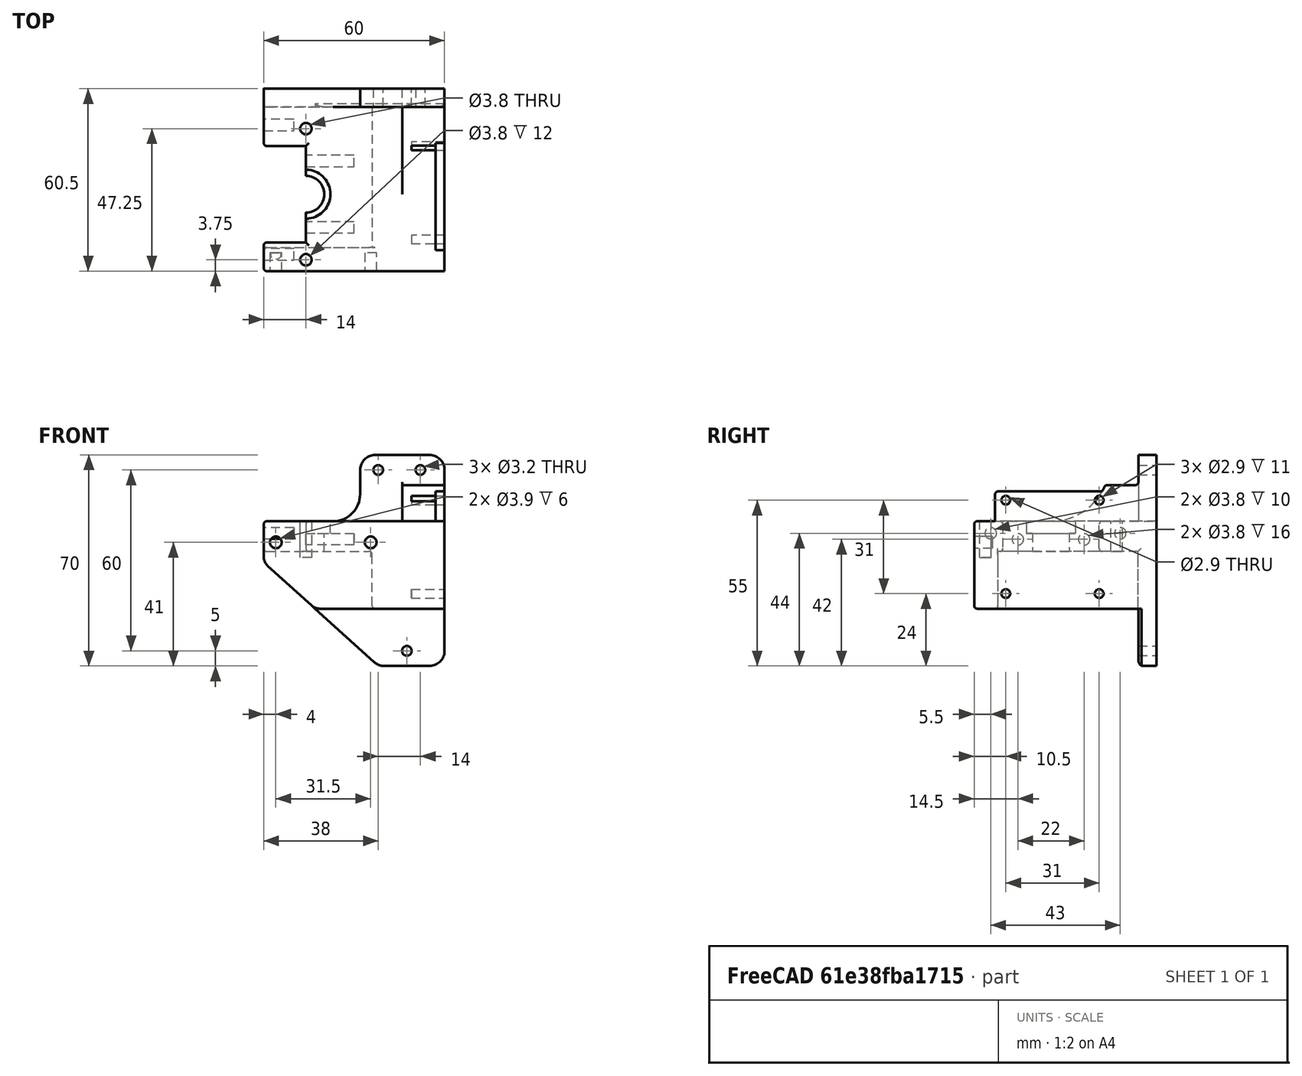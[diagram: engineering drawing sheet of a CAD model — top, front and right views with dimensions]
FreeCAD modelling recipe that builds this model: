
FCSTD DOCUMENT  (FreeCAD 0.19R)
Label: head9.3
License: All rights reserved
LicenseURL: http://en.wikipedia.org/wiki/All_rights_reserved
objects: PartDesign::Fillet×19, Sketcher::SketchObject×17, PartDesign::Pocket×15, PartDesign::Pad×2, PartDesign::Chamfer×1, PartDesign::Body×1, Mesh::Feature×1
note: 92 computed .brp shape members not serialized (recipe doc carries the construction recipe); baked Part::Feature solids carry a one-line shape summary decoded from their .brp

FEATURE [Sketcher::SketchObject] Sketch
  FullyConstrained = true
  MapMode = 5
  Support = -> [XY_Plane]
  sketch-geometry (5):
    g0: LineSegment StartX=0 StartY=0 StartZ=0 EndX=46 EndY=0 EndZ=0
    g1: LineSegment StartX=-14 StartY=0 StartZ=0 EndX=0 EndY=0 EndZ=0
    g2: LineSegment StartX=-14 StartY=0 StartZ=0 EndX=-14 EndY=-60.5 EndZ=0
    g3: LineSegment StartX=-14 StartY=-60.5 StartZ=0 EndX=46 EndY=-60.5 EndZ=0
    g4: LineSegment StartX=46 StartY=-60.5 StartZ=0 EndX=46 EndY=0 EndZ=0
  constraints (14):
    c: Coincident(g-1,g0)
    c: PointOnObject(g0,g-1)
    c: PointOnObject(g1,g-1)
    c: Coincident(g1,g0)
    c: Coincident(g1,g2)
    c: Vertical(g2)
    c: Coincident(g2,g3)
    c: Horizontal(g3)
    c: Coincident(g3,g4)
    c: Coincident(g4,g0)
    c: Vertical(g4)
    c: Distance(g4) = 60.5
    c: DistanceX(g0) = 46
    c: DistanceX(g1) = -14
FEATURE [PartDesign::Pad] Pad
  Direction = (1,1,1)
  Length = 70
  Length2 = 100
  Profile = -> Sketch
  Type = 0
FEATURE [Sketcher::SketchObject] Sketch002  label="platformnotch"
  FullyConstrained = false
  MapMode = 5
  Placement = pos=(0,0,70) rot=(0,0,1;0rad)
  Support = -> [Pad]
  sketch-geometry (6):
    g0: LineSegment StartX=32 StartY=-6 StartZ=0 EndX=32 EndY=-65.096 EndZ=0
    g1: LineSegment StartX=32 StartY=-65.096 StartZ=0 EndX=-40.7834 EndY=-65.096 EndZ=0
    g2: LineSegment StartX=-40.7834 StartY=-65.096 StartZ=0 EndX=-40.7834 EndY=12.9948 EndZ=0
    g3: LineSegment StartX=-40.7834 StartY=12.9948 StartZ=0 EndX=18 EndY=12.9948 EndZ=0
    g4: LineSegment StartX=18 StartY=12.9948 StartZ=0 EndX=18 EndY=-6 EndZ=0
    g5: LineSegment StartX=18 StartY=-6 StartZ=0 EndX=32 EndY=-6 EndZ=0
  constraints (15):
    c: Coincident(g0,g1)
    c: Coincident(g1,g2)
    c: Horizontal(g1)
    c: Vertical(g0)
    c: Vertical(g2)
    c: DistanceX(g0) = 32
    c: DistanceY(g0) = -6
    c: Coincident(g2,g3)
    c: Horizontal(g3)
    c: Coincident(g3,g4)
    c: Coincident(g4,g5)
    c: Coincident(g5,g0)
    c: Horizontal(g5)
    c: Vertical(g4)
    c: DistanceX(g3) = 18
FEATURE [PartDesign::Pocket] Pocket
  BaseFeature = -> Pad
  Length = 22
  Length2 = 100
  Profile = -> Sketch002
  Type = 0
FEATURE [Sketcher::SketchObject] Sketch008  label="pcbnotches"
  FullyConstrained = false
  MapMode = 5
  Placement = pos=(46,0,0) rot=(0.57735,0.57735,0.57735;2.0944rad)
  Support = -> [Pocket]
  sketch-geometry (8):
    g0: LineSegment StartX=-67.659 StartY=19 StartZ=0 EndX=-6 EndY=19 EndZ=0
    g1: LineSegment StartX=-6 StartY=19 StartZ=0 EndX=-6 EndY=-22.4626 EndZ=0
    g2: LineSegment StartX=-6 StartY=-22.4626 StartZ=0 EndX=-67.659 EndY=-22.4626 EndZ=0
    g3: LineSegment StartX=-67.659 StartY=-22.4626 StartZ=0 EndX=-67.659 EndY=19 EndZ=0
    g4: LineSegment StartX=-66.332 StartY=73.6841 StartZ=0 EndX=-6 EndY=73.6841 EndZ=0
    g5: LineSegment StartX=-6 StartY=73.6841 StartZ=0 EndX=-6 EndY=60 EndZ=0
    g6: LineSegment StartX=-6 StartY=60 StartZ=0 EndX=-66.332 EndY=60 EndZ=0
    g7: LineSegment StartX=-66.332 StartY=60 StartZ=0 EndX=-66.332 EndY=73.6841 EndZ=0
  constraints (20):
    c: Coincident(g0,g1)
    c: Coincident(g1,g2)
    c: Coincident(g2,g3)
    c: Coincident(g3,g0)
    c: Horizontal(g0)
    c: Horizontal(g2)
    c: Vertical(g1)
    c: Vertical(g3)
    c: DistanceY(g0) = 19
    c: Coincident(g4,g5)
    c: Coincident(g5,g6)
    c: Coincident(g6,g7)
    c: Coincident(g7,g4)
    c: Horizontal(g4)
    c: Horizontal(g6)
    c: Vertical(g5)
    c: Vertical(g7)
    c: DistanceX(g4) = -6
    c: DistanceY(g5) = 60
    c: DistanceX(g0) = -6
FEATURE [PartDesign::Pocket] Pocket001
  BaseFeature = -> Pocket
  Length = 76
  Length2 = 100
  Profile = -> Sketch008
  Type = 0
FEATURE [Sketcher::SketchObject] Sketch003  label="extredureholes"
  FullyConstrained = true
  MapMode = 5
  Placement = pos=(0,0,48) rot=(0,0,1;0rad)
  Support = -> [Pocket001]
  sketch-geometry (3):
    g0: Circle CenterX=0 CenterY=-13.25 CenterZ=0 NormalX=0 NormalY=0 NormalZ=1 AngleXU=0 Radius=1.9
    g1: Circle CenterX=0 CenterY=-56.75 CenterZ=0 NormalX=0 NormalY=0 NormalZ=1 AngleXU=0 Radius=1.9
    g2: LineSegment StartX=-14.87 StartY=-35 StartZ=0 EndX=14.87 EndY=-35 EndZ=0
  constraints (8):
    c: Distance(g1,g0) = 43.5
    c: Diameter(g1) = 3.8
    c: PointOnObject(g0,g-2)
    c: Symmetric(g2,g2,g-2)
    c: Distance(g2) = 29.74
    c: Symmetric(g1,g0,g2)
    c: DistanceY(g2) = -35
    c: Diameter(g0) = 3.8
FEATURE [PartDesign::Pocket] Pocket002
  BaseFeature = -> Pocket001
  Length = 12
  Length2 = 100
  Profile = -> Sketch003
  Type = 0
FEATURE [Sketcher::SketchObject] Sketch004  label="topNotch"
  FullyConstrained = true
  MapMode = 5
  Placement = pos=(0,0,48) rot=(0,0,1;0rad)
  Support = -> [Pocket002]
  sketch-geometry (4):
    g0: ArcOfCircle CenterX=0 CenterY=-35 CenterZ=0 NormalX=0 NormalY=0 NormalZ=1 AngleXU=0 Radius=8.125 StartAngle=4.71239 EndAngle=7.85398
    g1: LineSegment StartX=-1.5e-15 StartY=-43.125 StartZ=0 EndX=-25 EndY=-43.125 EndZ=0
    g2: LineSegment StartX=-25 StartY=-43.125 StartZ=0 EndX=-25 EndY=-26.875 EndZ=0
    g3: LineSegment StartX=-25 StartY=-26.875 StartZ=0 EndX=-2.629e-13 EndY=-26.875 EndZ=0
  constraints (11):
    c: PointOnObject(g0,g-2)
    c: Diameter(g0) = 16.25
    c: DistanceY(g0) = -35
    c: Coincident(g1,g2)
    c: Coincident(g2,g3)
    c: Distance(g3) = 25
    c: Tangent(g3,g0) = 1.5708
    c: Tangent(g1,g0) = 1.5708
    c: Horizontal(g3)
    c: Horizontal(g1)
    c: Vertical(g2)
FEATURE [PartDesign::Pocket] Pocket003
  BaseFeature = -> Pocket002
  Length = 4
  Length2 = 100
  Profile = -> Sketch004
  Type = 0
FEATURE [Sketcher::SketchObject] Sketch018  label="innergroove"
  FullyConstrained = true
  MapMode = 5
  Placement = pos=(0,0,44) rot=(0,0,1;0rad)
  Support = -> [Pocket003]
  sketch-geometry (4):
    g0: ArcOfCircle CenterX=0 CenterY=-35 CenterZ=0 NormalX=0 NormalY=0 NormalZ=1 AngleXU=0 Radius=6.1 StartAngle=4.71239 EndAngle=7.85398
    g1: LineSegment StartX=-1.1e-15 StartY=-41.1 StartZ=0 EndX=-50 EndY=-41.1 EndZ=0
    g2: LineSegment StartX=1.9e-15 StartY=-28.9 StartZ=0 EndX=-50 EndY=-28.9 EndZ=0
    g3: LineSegment StartX=-50 StartY=-41.1 StartZ=0 EndX=-50 EndY=-28.9 EndZ=0
  constraints (11):
    c: PointOnObject(g0,g-2)
    c: Coincident(g3,g1)
    c: Coincident(g3,g2)
    c: Tangent(g1,g0) = 1.5708
    c: Tangent(g2,g0) = -1.5708
    c: DistanceY(g0) = -35
    c: Diameter(g0) = 12.2
    c: Distance(g1) = 50
    c: Vertical(g3)
    c: Horizontal(g1)
    c: Horizontal(g2)
FEATURE [PartDesign::Pocket] Pocket004
  BaseFeature = -> Pocket003
  Length = 6
  Length2 = 100
  Profile = -> Sketch018
  Type = 0
FEATURE [Sketcher::SketchObject] Sketch009  label="PCBholes"
  FullyConstrained = true
  MapMode = 5
  Placement = pos=(46,0,0) rot=(0.57735,0.57735,0.57735;2.0944rad)
  Support = -> [Pocket004]
  sketch-geometry (5):
    g0: Circle CenterX=-50 CenterY=55 CenterZ=0 NormalX=0 NormalY=0 NormalZ=1 AngleXU=0 Radius=1.35
    g1: Circle CenterX=-19 CenterY=24 CenterZ=0 NormalX=0 NormalY=0 NormalZ=1 AngleXU=0 Radius=1.35
    g2: LineSegment StartX=-50 StartY=55 StartZ=0 EndX=-19 EndY=24 EndZ=0
    g3: Circle CenterX=-19 CenterY=55 CenterZ=0 NormalX=0 NormalY=0 NormalZ=1 AngleXU=0 Radius=1.35
    g4: Circle CenterX=-50 CenterY=24 CenterZ=0 NormalX=0 NormalY=0 NormalZ=1 AngleXU=0 Radius=1.35
  constraints (14):
    c: Coincident(g2,g0)
    c: Coincident(g2,g1)
    c: Angle(g2) = -0.785398
    c: DistanceX(g1) = -19
    c: DistanceY(g1) = 24
    c: Diameter(g4) = 2.7
    c: Equal(g4,g0)
    c: Equal(g4,g3)
    c: Equal(g4,g1)
    c: DistanceY(g4,g0) = 31
    c: DistanceX(g0,g3) = 31
    c: DistanceX(g4,g1) = 31
    c: DistanceY(g4) = 24
    c: DistanceY(g1,g3) = 31
FEATURE [PartDesign::Pocket] Pocket005
  BaseFeature = -> Pocket004
  Length = 10
  Length2 = 100
  Profile = -> Sketch009
  Type = 0
FEATURE [Sketcher::SketchObject] Sketch030
  FullyConstrained = false
  MapMode = 5
  Placement = pos=(0,0,48) rot=(0,0,1;0rad)
  Support = -> [Pocket005]
  sketch-geometry (5):
    g0: LineSegment StartX=-28.769 StartY=-19 StartZ=0 EndX=0 EndY=-19 EndZ=0
    g1: LineSegment StartX=0 StartY=-19 StartZ=0 EndX=0 EndY=-51 EndZ=0
    g2: LineSegment StartX=0 StartY=-51 StartZ=0 EndX=-28.769 EndY=-51 EndZ=0
    g3: LineSegment StartX=-28.769 StartY=-51 StartZ=0 EndX=-28.769 EndY=-19 EndZ=0
    g4: LineSegment StartX=-7.77915 StartY=-35 StartZ=0 EndX=15.2351 EndY=-35 EndZ=0
  constraints (12):
    c: Coincident(g0,g1)
    c: Coincident(g1,g2)
    c: Coincident(g2,g3)
    c: Coincident(g3,g0)
    c: Horizontal(g0)
    c: Horizontal(g2)
    c: Vertical(g1)
    c: Vertical(g3)
    c: PointOnObject(g1,g-2)
    c: Distance(g1) = 32
    c: Symmetric(g0,g1,g4)
    c: DistanceY(g4) = -35
FEATURE [PartDesign::Pocket] Pocket006
  BaseFeature = -> Pocket005
  Length = 5
  Length2 = 100
  Profile = -> Sketch030
  Type = 1
FEATURE [Sketcher::SketchObject] Sketch031
  FullyConstrained = false
  MapMode = 5
  Placement = pos=(-14,0,0) rot=(0.57735,-0.57735,-0.57735;2.0944rad)
  Support = -> [Pocket006]
  sketch-geometry (4):
    g0: LineSegment StartX=6.1 StartY=38 StartZ=0 EndX=52.7193 EndY=38 EndZ=0
    g1: LineSegment StartX=52.7193 StartY=38 StartZ=0 EndX=52.7193 EndY=2.95128 EndZ=0
    g2: LineSegment StartX=52.7193 StartY=2.95128 StartZ=0 EndX=6.1 EndY=2.95128 EndZ=0
    g3: LineSegment StartX=6.1 StartY=2.95128 StartZ=0 EndX=6.1 EndY=38 EndZ=0
  constraints (10):
    c: Coincident(g0,g1)
    c: Coincident(g1,g2)
    c: Coincident(g2,g3)
    c: Coincident(g3,g0)
    c: Horizontal(g0)
    c: Horizontal(g2)
    c: Vertical(g1)
    c: Vertical(g3)
    c: DistanceX(g0) = 6.1
    c: DistanceY(g0) = 38
FEATURE [PartDesign::Pocket] Pocket007
  BaseFeature = -> Pocket006
  Length = 36
  Length2 = 100
  Profile = -> Sketch031
  Type = 0
FEATURE [Sketcher::SketchObject] Sketch032  label="FanScrews"
  ExternalGeometry = -> [Pocket007]
  FullyConstrained = true
  MapMode = 5
  Placement = pos=(-14,0,0) rot=(0.57735,-0.57735,-0.57735;2.0944rad)
  Support = -> [Pocket007]
  sketch-geometry (2):
    g0: Circle CenterX=12 CenterY=44 CenterZ=0 NormalX=0 NormalY=0 NormalZ=1 AngleXU=0 Radius=1.9
    g1: Circle CenterX=55 CenterY=44 CenterZ=0 NormalX=0 NormalY=0 NormalZ=1 AngleXU=0 Radius=1.9
  constraints (6):
    c: Diameter(g0) = 3.8
    c: DistanceX(g0) = 12
    c: DistanceY(g0) = 44
    c: Diameter(g1) = 3.8
    c: DistanceY(g1) = 44
    c: DistanceX(g1) = 55
FEATURE [PartDesign::Pocket] Pocket008
  BaseFeature = -> Pocket007
  Length = 10
  Length2 = 100
  Profile = -> Sketch032
  Type = 0
FEATURE [Sketcher::SketchObject] Sketch013  label="groovescrews"
  FullyConstrained = false
  MapMode = 5
  Placement = pos=(0,0,0) rot=(0.57735,-0.57735,-0.57735;2.0944rad)
  Support = -> [Pocket008]
  sketch-geometry (3):
    g0: Circle CenterX=24 CenterY=42 CenterZ=0 NormalX=0 NormalY=0 NormalZ=1 AngleXU=0 Radius=1.9
    g1: Circle CenterX=46 CenterY=42 CenterZ=0 NormalX=0 NormalY=0 NormalZ=1 AngleXU=0 Radius=1.9
    g2: LineSegment StartX=35 StartY=87.2769 StartZ=0 EndX=35 EndY=69.6255 EndZ=0
  constraints (6):
    c: Distance(g1,g0) = 22
    c: Diameter(g1) = 3.8
    c: Equal(g1,g0)
    c: Vertical(g2)
    c: Symmetric(g1,g0,g2)
    c: DistanceX(g2) = 35
FEATURE [PartDesign::Pocket] Pocket009
  BaseFeature = -> Pocket008
  Length = 16
  Length2 = 100
  Profile = -> Sketch013
  Type = 0
FEATURE [Sketcher::SketchObject] Sketch010  label="mountholes"
  FullyConstrained = true
  MapMode = 5
  Placement = pos=(0,0,0) rot=(0,0.707107,0.707107;3.14159rad)
  Support = -> [Pocket009]
  sketch-geometry (3):
    g0: Circle CenterX=-33.5 CenterY=5 CenterZ=0 NormalX=0 NormalY=0 NormalZ=1 AngleXU=0 Radius=1.6
    g1: Circle CenterX=-38 CenterY=65 CenterZ=0 NormalX=0 NormalY=0 NormalZ=1 AngleXU=0 Radius=1.6
    g2: Circle CenterX=-24 CenterY=65 CenterZ=0 NormalX=0 NormalY=0 NormalZ=1 AngleXU=0 Radius=1.6
  constraints (9):
    c: Diameter(g0) = 3.2
    c: Equal(g0,g2)
    c: Equal(g0,g1)
    c: DistanceX(g0) = -33.5
    c: Distance(g1,g2) = 14
    c: DistanceX(g2) = -24
    c: DistanceY(g0) = 5
    c: DistanceY(g2) = 65
    c: DistanceY(g1) = 65
FEATURE [PartDesign::Pocket] Pocket010
  BaseFeature = -> Pocket009
  Length = 7
  Length2 = 100
  Profile = -> Sketch010
  Type = 0
FEATURE [Sketcher::SketchObject] Sketch033  label="ANgler"
  FullyConstrained = false
  MapMode = 5
  Placement = pos=(0,0,0) rot=(0,0.707107,0.707107;3.14159rad)
  Support = -> [Pocket010]
  sketch-geometry (3):
    g0: LineSegment StartX=21.9958 StartY=41.6537 StartZ=0 EndX=-34.9081 EndY=-9.83073 EndZ=0
    g1: LineSegment StartX=21.9958 StartY=41.6537 StartZ=0 EndX=21.9958 EndY=-12.4114 EndZ=0
    g2: LineSegment StartX=21.9958 StartY=-12.4114 StartZ=0 EndX=-34.9081 EndY=-9.83073 EndZ=0
  constraints (4):
    c: Coincident(g0,g1)
    c: Vertical(g1)
    c: Coincident(g1,g2)
    c: Coincident(g2,g0)
FEATURE [PartDesign::Pocket] Pocket011
  BaseFeature = -> Pocket010
  Length = 5
  Length2 = 100
  Profile = -> Sketch033
  Type = 1
FEATURE [Sketcher::SketchObject] Sketch034
  ExternalGeometry = -> [Pocket011]
  FullyConstrained = true
  MapMode = 5
  Placement = pos=(32,0,0) rot=(0.57735,-0.57735,-0.57735;2.0944rad)
  Support = -> [Pocket011]
  sketch-geometry (4):
    g0: ArcOfCircle CenterX=35 CenterY=67.5 CenterZ=0 NormalX=0 NormalY=0 NormalZ=1 AngleXU=0 Radius=19.5 StartAngle=3.14159 EndAngle=4.71239
    g1: LineSegment StartX=35 StartY=48 StartZ=0 EndX=74.47 EndY=48 EndZ=0
    g2: LineSegment StartX=15.5 StartY=67.5 StartZ=0 EndX=74.47 EndY=67.5 EndZ=0
    g3: LineSegment StartX=74.47 StartY=67.5 StartZ=0 EndX=74.47 EndY=48 EndZ=0
  constraints (13):
    c: DistanceX(g0) = 35
    c: Diameter(g0) = 39
    c: Coincident(g1,g0)
    c: Horizontal(g1)
    c: Coincident(g0,g2)
    c: Coincident(g2,g3)
    c: Coincident(g3,g1)
    c: Horizontal(g2)
    c: Perpendicular(g0,g2)
    c: PointOnObject(g-3,g1)
    c: Vertical(g3)
    c: Distance(g2) = 58.97
    c: DistanceX(g0) = 35
FEATURE [PartDesign::Pocket] Pocket012
  BaseFeature = -> Pocket011
  Length = 10
  Length2 = 100
  Profile = -> Sketch034
  Type = 1
FEATURE [Sketcher::SketchObject] Sketch035  label="FrontMountHoles"
  ExternalGeometry = -> [Pocket012]
  FullyConstrained = false
  MapMode = 5
  Placement = pos=(0,-60.5,0) rot=(1,0,0;1.5708rad)
  Support = -> [Pocket012]
  sketch-geometry (3):
    g0: Circle CenterX=-10 CenterY=41 CenterZ=0 NormalX=0 NormalY=0 NormalZ=1 AngleXU=0 Radius=1.95
    g1: Circle CenterX=21.5 CenterY=41 CenterZ=0 NormalX=0 NormalY=0 NormalZ=1 AngleXU=0 Radius=1.95
    g2: LineSegment StartX=-4.95622 StartY=-23 StartZ=0 EndX=5.01253 EndY=-23 EndZ=0
  constraints (8):
    c: Diameter(g1) = 3.9
    c: Equal(g1,g0)
    c: DistanceX(g0,g-1) = 10
    c: Distance(g1,g0) = 31.5
    c: Horizontal(g2)
    c: Distance(g2,g-3) = 71
    c: Distance(g1,g2) = 64
    c: Distance(g0,g2) = 64
FEATURE [PartDesign::Pocket] Pocket013
  BaseFeature = -> Pocket012
  Length = 6
  Length2 = 100
  Profile = -> Sketch035
  Type = 0
FEATURE [PartDesign::Fillet] Fillet
  Base = -> Pocket013 [Edge32]
  BaseFeature = -> Pocket013
  Radius = 9
  SupportTransform = false
FEATURE [PartDesign::Fillet] Fillet001
  Base = -> Fillet [Edge15,Edge20,Edge38,Edge51]
  BaseFeature = -> Fillet
  Radius = 5
  SupportTransform = false
FEATURE [PartDesign::Fillet] Fillet002
  Base = -> Fillet001 [Edge61]
  BaseFeature = -> Fillet001
  Radius = 4
  SupportTransform = false
FEATURE [PartDesign::Fillet] Fillet003
  Base = -> Fillet002 [Edge124]
  BaseFeature = -> Fillet002
  Radius = 4
  SupportTransform = false
FEATURE [PartDesign::Fillet] Fillet004
  Base = -> Fillet003 [Edge11]
  BaseFeature = -> Fillet003
  Radius = 4
  SupportTransform = false
FEATURE [PartDesign::Fillet] Fillet005
  Base = -> Fillet004 [Edge19]
  BaseFeature = -> Fillet004
  Radius = 1
  SupportTransform = false
FEATURE [PartDesign::Fillet] Fillet006
  Base = -> Fillet005 [Edge57]
  BaseFeature = -> Fillet005
  Radius = 1
  SupportTransform = false
FEATURE [Sketcher::SketchObject] Sketch036
  FullyConstrained = false
  MapMode = 5
  Placement = pos=(46,0,0) rot=(0.57735,0.57735,0.57735;2.0944rad)
  Support = -> [Fillet006]
  sketch-geometry (4):
    g0: LineSegment StartX=-53.5397 StartY=57.9121 StartZ=0 EndX=-16.5185 EndY=57.9121 EndZ=0
    g1: LineSegment StartX=-16.5185 StartY=57.9121 StartZ=0 EndX=-16.5185 EndY=21.9397 EndZ=0
    g2: LineSegment StartX=-16.5185 StartY=21.9397 StartZ=0 EndX=-53.5397 EndY=21.9397 EndZ=0
    g3: LineSegment StartX=-53.5397 StartY=21.9397 StartZ=0 EndX=-53.5397 EndY=57.9121 EndZ=0
  constraints (8):
    c: Coincident(g0,g1)
    c: Coincident(g1,g2)
    c: Coincident(g2,g3)
    c: Coincident(g3,g0)
    c: Horizontal(g0)
    c: Horizontal(g2)
    c: Vertical(g1)
    c: Vertical(g3)
FEATURE [PartDesign::Pad] Pad001
  BaseFeature = -> Fillet006
  Direction = (1,1,1)
  Length = 3
  Length2 = 100
  Profile = -> Sketch036
  Reversed = true
  Type = 0
FEATURE [Sketcher::SketchObject] Sketch037
  ExternalGeometry = -> [Pad001]
  FullyConstrained = true
  MapMode = 5
  Placement = pos=(46,0,0) rot=(0.57735,0.57735,0.57735;2.0944rad)
  Support = -> [Pad001]
  sketch-geometry (4):
    g0: Circle CenterX=-19 CenterY=55 CenterZ=0 NormalX=0 NormalY=0 NormalZ=1 AngleXU=0 Radius=1.45
    g1: Circle CenterX=-19 CenterY=24 CenterZ=0 NormalX=0 NormalY=0 NormalZ=1 AngleXU=0 Radius=1.45
    g2: Circle CenterX=-50 CenterY=24 CenterZ=0 NormalX=0 NormalY=0 NormalZ=1 AngleXU=0 Radius=1.45
    g3: Circle CenterX=-50 CenterY=55 CenterZ=0 NormalX=0 NormalY=0 NormalZ=1 AngleXU=0 Radius=1.45
  constraints (9):
    c: Diameter(g2) = 2.9
    c: Equal(g2,g3)
    c: Equal(g2,g0)
    c: Equal(g2,g1)
    c: Coincident(g-5,g2)
    c: Coincident(g1,g-3)
    c: Coincident(g0,g-4)
    c: Distance(g3,g0) = 31
    c: Distance(g2,g3) = 31
FEATURE [PartDesign::Pocket] Pocket014
  BaseFeature = -> Pad001
  Length = 11
  Length2 = 100
  Profile = -> Sketch037
  Type = 0
FEATURE [PartDesign::Fillet] Fillet007
  Base = -> Pocket014 [Edge91]
  BaseFeature = -> Pocket014
  Radius = 1
  SupportTransform = false
FEATURE [PartDesign::Fillet] Fillet008
  Base = -> Fillet007 [Edge170]
  BaseFeature = -> Fillet007
  Radius = 1
  SupportTransform = false
FEATURE [PartDesign::Fillet] Fillet009
  Base = -> Fillet008 [Edge20]
  BaseFeature = -> Fillet008
  Radius = 1
  SupportTransform = false
FEATURE [PartDesign::Fillet] Fillet010
  Base = -> Fillet009 [Edge63]
  BaseFeature = -> Fillet009
  Radius = 1
  SupportTransform = false
FEATURE [PartDesign::Fillet] Fillet011
  Base = -> Fillet010 [Edge40,Edge123]
  BaseFeature = -> Fillet010
  Radius = 1
  SupportTransform = false
FEATURE [PartDesign::Fillet] Fillet012
  Base = -> Fillet011 [Edge66,Edge12]
  BaseFeature = -> Fillet011
  Radius = 1
  SupportTransform = false
FEATURE [PartDesign::Fillet] Fillet013
  Base = -> Fillet012 [Edge114]
  BaseFeature = -> Fillet012
  Radius = 1
  SupportTransform = false
FEATURE [PartDesign::Fillet] Fillet014
  Base = -> Fillet013 [Edge70]
  BaseFeature = -> Fillet013
  Radius = 1
  SupportTransform = false
FEATURE [PartDesign::Fillet] Fillet015
  Base = -> Fillet014 [Edge5,Edge9]
  BaseFeature = -> Fillet014
  Radius = 1
  SupportTransform = false
FEATURE [PartDesign::Fillet] Fillet016
  Base = -> Fillet015 [Edge94,Edge86]
  BaseFeature = -> Fillet015
  Radius = 1
  SupportTransform = false
FEATURE [PartDesign::Chamfer] Chamfer
  Angle = 45
  Base = -> Fillet016 [Edge233]
  BaseFeature = -> Fillet016
  ChamferType = 0
  FlipDirection = false
  Size = 1
  Size2 = 1
  SupportTransform = false
FEATURE [PartDesign::Fillet] Fillet017
  Base = -> Chamfer [Edge16]
  BaseFeature = -> Chamfer
  Radius = 2
  SupportTransform = false
FEATURE [PartDesign::Fillet] Fillet018
  Base = -> Fillet017 [Edge51]
  BaseFeature = -> Fillet017
  Radius = 1
  SupportTransform = false
FEATURE [PartDesign::Body] Body
  Group = -> [Sketch,Pad,Sketch002,Sketch003,Sketch004,Sketch008,Sketch009,Sketch010,Sketch013,Sketch018,Pocket,Pocket001,Pocket002,Pocket003,Pocket004,Pocket005,Sketch030,Pocket006,Sketch031,Pocket007,Sketch032,Pocket008,Pocket009,Pocket010,Sketch033,Pocket011,Sketch034,Pocket012,Sketch035,Pocket013,Fillet,Fillet001,Fillet002,Fillet003,Fillet004,Fillet005,Fillet006,Sketch036,Pad001,Sketch037,Pocket014,+13 more]
  Origin = -> Origin
  Tip = -> Fillet018
FEATURE [Mesh::Feature] Mesh  label="Fillet018 (Meshed)"
